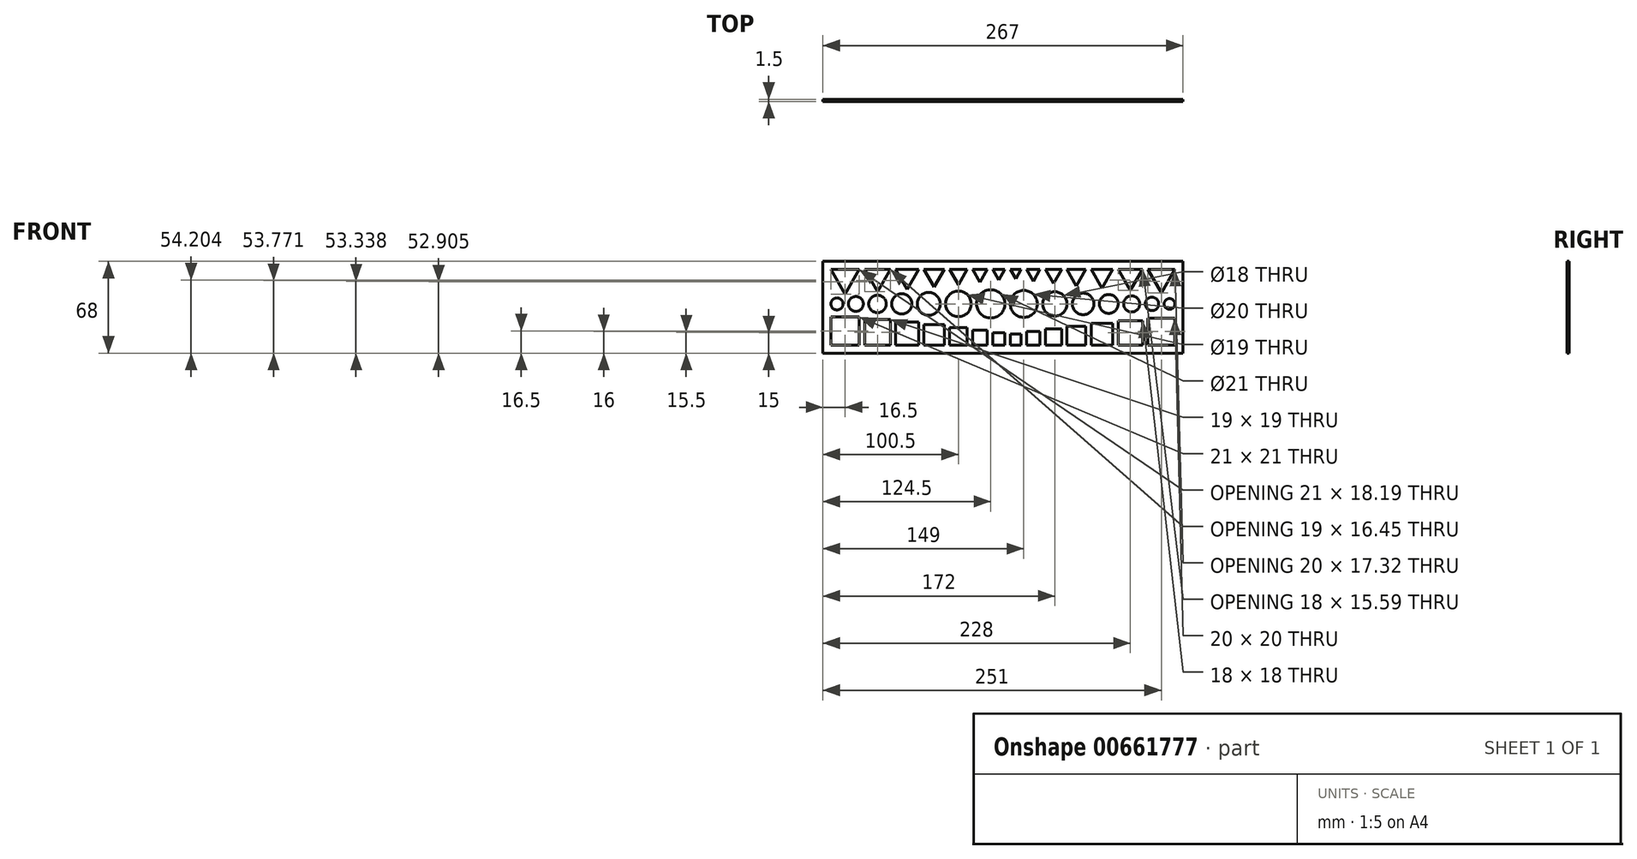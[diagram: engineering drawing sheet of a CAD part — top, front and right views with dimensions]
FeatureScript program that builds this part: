
annotation { "Feature Type Name" : "Feature", "Feature Type Description" : "" }
export const myFeature = defineFeature(function(context is Context, id is Id, definition is map)
    precondition{}
    {
        {
            var Q0;
            Q0=qCreatedBy(makeId("Front.planeOp"),FACE);
            var sketch = newSketch(context, id + "F0", { "sketchPlane" : qUnion([Q0])});
            skLineSegment(sketch, "E0.bottom", {"start": v(0, 0) * mm, "end": v(8, 0) * mm});
            skLineSegment(sketch, "E0.top", {"start": v(0, 8) * mm, "end": v(8, 8) * mm});
            skLineSegment(sketch, "E0.left", {"start": v(0, 0) * mm, "end": v(0, 8) * mm});
            skLineSegment(sketch, "E0.right", {"start": v(8, 0) * mm, "end": v(8, 8) * mm});
            skLineSegment(sketch, "E1.bottom", {"start": v(12, 0) * mm, "end": v(22, 0) * mm});
            skLineSegment(sketch, "E1.top", {"start": v(12, 10) * mm, "end": v(22, 10) * mm});
            skLineSegment(sketch, "E1.left", {"start": v(12, 0) * mm, "end": v(12, 10) * mm});
            skLineSegment(sketch, "E1.right", {"start": v(22, 0) * mm, "end": v(22, 10) * mm});
            skLineSegment(sketch, "E2.bottom", {"start": v(26, 0) * mm, "end": v(38, 0) * mm});
            skLineSegment(sketch, "E2.top", {"start": v(26, 12) * mm, "end": v(38, 12) * mm});
            skLineSegment(sketch, "E2.left", {"start": v(26, 0) * mm, "end": v(26, 12) * mm});
            skLineSegment(sketch, "E2.right", {"start": v(38, 0) * mm, "end": v(38, 12) * mm});
            skLineSegment(sketch, "E3.bottom", {"start": v(42, 0) * mm, "end": v(56, 0) * mm});
            skLineSegment(sketch, "E3.top", {"start": v(42, 14) * mm, "end": v(56, 14) * mm});
            skLineSegment(sketch, "E3.left", {"start": v(42, 0) * mm, "end": v(42, 14) * mm});
            skLineSegment(sketch, "E3.right", {"start": v(56, 0) * mm, "end": v(56, 14) * mm});
            skLineSegment(sketch, "E4.bottom", {"start": v(60, 0) * mm, "end": v(76, 0) * mm});
            skLineSegment(sketch, "E4.top", {"start": v(60, 16) * mm, "end": v(76, 16) * mm});
            skLineSegment(sketch, "E4.left", {"start": v(60, 0) * mm, "end": v(60, 16) * mm});
            skLineSegment(sketch, "E4.right", {"start": v(76, 0) * mm, "end": v(76, 16) * mm});
            skLineSegment(sketch, "E5.bottom", {"start": v(80, 0) * mm, "end": v(98, 0) * mm});
            skLineSegment(sketch, "E5.top", {"start": v(80, 18) * mm, "end": v(98, 18) * mm});
            skLineSegment(sketch, "E5.left", {"start": v(80, 0) * mm, "end": v(80, 18) * mm});
            skLineSegment(sketch, "E5.right", {"start": v(98, 0) * mm, "end": v(98, 18) * mm});
            skLineSegment(sketch, "E6.bottom", {"start": v(102, 0) * mm, "end": v(122, 0) * mm});
            skLineSegment(sketch, "E6.top", {"start": v(102, 20) * mm, "end": v(122, 20) * mm});
            skLineSegment(sketch, "E6.left", {"start": v(102, 0) * mm, "end": v(102, 20) * mm});
            skLineSegment(sketch, "E6.right", {"start": v(122, 0) * mm, "end": v(122, 20) * mm});
            skCircle(sketch, "E7", {"center": v(118, 30.5) * mm, "radius": 4 * mm});
            skCircle(sketch, "E8", {"center": v(105, 30.5) * mm, "radius": 5 * mm});
            skCircle(sketch, "E9", {"center": v(73, 30.5) * mm, "radius": 7 * mm});
            skCircle(sketch, "E10", {"center": v(90, 30.5) * mm, "radius": 6 * mm});
            skCircle(sketch, "E11", {"center": v(54, 30.5) * mm, "radius": 8 * mm});
            skCircle(sketch, "E12", {"center": v(33, 30.5) * mm, "radius": 9 * mm});
            skCircle(sketch, "E13", {"center": v(10, 30.5) * mm, "radius": 10 * mm});
            skLineSegment(sketch, "E14.bottom", {"start": v(-4, 0) * mm, "end": v(-13, 0) * mm});
            skLineSegment(sketch, "E14.top", {"start": v(-4, 9) * mm, "end": v(-13, 9) * mm});
            skLineSegment(sketch, "E14.left", {"start": v(-4, 0) * mm, "end": v(-4, 9) * mm});
            skLineSegment(sketch, "E14.right", {"start": v(-13, 0) * mm, "end": v(-13, 9) * mm});
            skLineSegment(sketch, "E15.bottom", {"start": v(-17, 0) * mm, "end": v(-28, 0) * mm});
            skLineSegment(sketch, "E15.top", {"start": v(-17, 11) * mm, "end": v(-28, 11) * mm});
            skLineSegment(sketch, "E15.left", {"start": v(-17, 0) * mm, "end": v(-17, 11) * mm});
            skLineSegment(sketch, "E15.right", {"start": v(-28, 0) * mm, "end": v(-28, 11) * mm});
            skLineSegment(sketch, "E16.bottom", {"start": v(-32, 0) * mm, "end": v(-45, 0) * mm});
            skLineSegment(sketch, "E16.top", {"start": v(-32, 13) * mm, "end": v(-45, 13) * mm});
            skLineSegment(sketch, "E16.left", {"start": v(-32, 0) * mm, "end": v(-32, 13) * mm});
            skLineSegment(sketch, "E16.right", {"start": v(-45, 0) * mm, "end": v(-45, 13) * mm});
            skLineSegment(sketch, "E17.bottom", {"start": v(-49, 0) * mm, "end": v(-64, 0) * mm});
            skLineSegment(sketch, "E17.top", {"start": v(-49, 15) * mm, "end": v(-64, 15) * mm});
            skLineSegment(sketch, "E17.left", {"start": v(-49, 0) * mm, "end": v(-49, 15) * mm});
            skLineSegment(sketch, "E17.right", {"start": v(-64, 0) * mm, "end": v(-64, 15) * mm});
            skLineSegment(sketch, "E18.bottom", {"start": v(-68, 0) * mm, "end": v(-85, 0) * mm});
            skLineSegment(sketch, "E18.top", {"start": v(-68, 17) * mm, "end": v(-85, 17) * mm});
            skLineSegment(sketch, "E18.left", {"start": v(-68, 0) * mm, "end": v(-68, 17) * mm});
            skLineSegment(sketch, "E18.right", {"start": v(-85, 0) * mm, "end": v(-85, 17) * mm});
            skLineSegment(sketch, "E19.bottom", {"start": v(-89, 0) * mm, "end": v(-108, 0) * mm});
            skLineSegment(sketch, "E19.top", {"start": v(-89, 19) * mm, "end": v(-108, 19) * mm});
            skLineSegment(sketch, "E19.left", {"start": v(-89, 0) * mm, "end": v(-89, 19) * mm});
            skLineSegment(sketch, "E19.right", {"start": v(-108, 0) * mm, "end": v(-108, 19) * mm});
            skLineSegment(sketch, "E20.bottom", {"start": v(-112, 0) * mm, "end": v(-133, 0) * mm});
            skLineSegment(sketch, "E20.top", {"start": v(-112, 21) * mm, "end": v(-133, 21) * mm});
            skLineSegment(sketch, "E20.left", {"start": v(-112, 0) * mm, "end": v(-112, 21) * mm});
            skLineSegment(sketch, "E20.right", {"start": v(-133, 0) * mm, "end": v(-133, 21) * mm});
            skCircle(sketch, "E21", {"center": v(-38.5, 30.5) * mm, "radius": 9.5 * mm});
            skCircle(sketch, "E22", {"center": v(-60.5, 30.5) * mm, "radius": 8.5 * mm});
            skCircle(sketch, "E23", {"center": v(-80.5, 30.5) * mm, "radius": 7.5 * mm});
            skCircle(sketch, "E24", {"center": v(-128.5, 30.5) * mm, "radius": 4.5 * mm});
            skCircle(sketch, "E25", {"center": v(-98.5, 30.5) * mm, "radius": 6.5 * mm});
            skCircle(sketch, "E26", {"center": v(-114.5, 30.5) * mm, "radius": 5.5 * mm});
            skCircle(sketch, "E27", {"center": v(-14.5, 30.5) * mm, "radius": 10.5 * mm});
            skCircle(sketch, "E28.cCircle", {"center": v(4, 53.69) * mm, "radius": 2.3 * mm, "construction": true});
            skLineSegment(sketch, "E28.0", {"start": v(0, 56) * mm, "end": v(8, 56) * mm});
            skLineSegment(sketch, "E28.1", {"start": v(8, 56) * mm, "end": v(4, 49.07) * mm});
            skLineSegment(sketch, "E28.2", {"start": v(4, 49.07) * mm, "end": v(0, 56) * mm});
            skPoint(sketch, "E28.0.midPoint", {"position": v(4, 56) * mm});
            skCircle(sketch, "E29.cCircle", {"center": v(17, 53.11) * mm, "radius": 2.89 * mm, "construction": true});
            skLineSegment(sketch, "E29.0", {"start": v(12, 56) * mm, "end": v(22, 56) * mm});
            skLineSegment(sketch, "E29.1", {"start": v(22, 56) * mm, "end": v(17, 47.34) * mm});
            skLineSegment(sketch, "E29.2", {"start": v(17, 47.34) * mm, "end": v(12, 56) * mm});
            skPoint(sketch, "E29.0.midPoint", {"position": v(17, 56) * mm});
            skCircle(sketch, "E30.cCircle", {"center": v(32, 52.53) * mm, "radius": 3.46 * mm, "construction": true});
            skLineSegment(sketch, "E30.0", {"start": v(26, 56) * mm, "end": v(38, 56) * mm});
            skLineSegment(sketch, "E30.1", {"start": v(38, 56) * mm, "end": v(32, 45.6) * mm});
            skLineSegment(sketch, "E30.2", {"start": v(32, 45.6) * mm, "end": v(26, 56) * mm});
            skPoint(sketch, "E30.0.midPoint", {"position": v(32, 56) * mm});
            skCircle(sketch, "E31.cCircle", {"center": v(49, 51.96) * mm, "radius": 4.04 * mm, "construction": true});
            skLineSegment(sketch, "E31.0", {"start": v(42, 56) * mm, "end": v(56, 56) * mm});
            skLineSegment(sketch, "E31.1", {"start": v(56, 56) * mm, "end": v(49, 43.87) * mm});
            skLineSegment(sketch, "E31.2", {"start": v(49, 43.87) * mm, "end": v(42, 56) * mm});
            skPoint(sketch, "E31.0.midPoint", {"position": v(49, 56) * mm});
            skCircle(sketch, "E32.cCircle", {"center": v(68, 51.38) * mm, "radius": 4.62 * mm, "construction": true});
            skLineSegment(sketch, "E32.0", {"start": v(60, 56) * mm, "end": v(76, 56) * mm});
            skLineSegment(sketch, "E32.1", {"start": v(76, 56) * mm, "end": v(68, 42.14) * mm});
            skLineSegment(sketch, "E32.2", {"start": v(68, 42.14) * mm, "end": v(60, 56) * mm});
            skPoint(sketch, "E32.0.midPoint", {"position": v(68, 56) * mm});
            skCircle(sketch, "E33.cCircle", {"center": v(89, 50.8) * mm, "radius": 5.2 * mm, "construction": true});
            skLineSegment(sketch, "E33.0", {"start": v(80, 56) * mm, "end": v(98, 56) * mm});
            skLineSegment(sketch, "E33.1", {"start": v(98, 56) * mm, "end": v(89, 40.4) * mm});
            skLineSegment(sketch, "E33.2", {"start": v(89, 40.4) * mm, "end": v(80, 56) * mm});
            skPoint(sketch, "E33.0.midPoint", {"position": v(89, 56) * mm});
            skCircle(sketch, "E34.cCircle", {"center": v(112, 50.22) * mm, "radius": 5.77 * mm, "construction": true});
            skLineSegment(sketch, "E34.0", {"start": v(102, 56) * mm, "end": v(122, 56) * mm});
            skLineSegment(sketch, "E34.1", {"start": v(122, 56) * mm, "end": v(112, 38.68) * mm});
            skLineSegment(sketch, "E34.2", {"start": v(112, 38.68) * mm, "end": v(102, 56) * mm});
            skPoint(sketch, "E34.0.midPoint", {"position": v(112, 56) * mm});
            skCircle(sketch, "E35.cCircle", {"center": v(-8.5, 53.4) * mm, "radius": 2.6 * mm, "construction": true});
            skLineSegment(sketch, "E35.0", {"start": v(-13, 56) * mm, "end": v(-4, 56) * mm});
            skLineSegment(sketch, "E35.1", {"start": v(-4, 56) * mm, "end": v(-8.5, 48.2) * mm});
            skLineSegment(sketch, "E35.2", {"start": v(-8.5, 48.2) * mm, "end": v(-13, 56) * mm});
            skPoint(sketch, "E35.0.midPoint", {"position": v(-8.5, 56) * mm});
            skCircle(sketch, "E36.cCircle", {"center": v(-22.5, 52.82) * mm, "radius": 3.18 * mm, "construction": true});
            skLineSegment(sketch, "E36.0", {"start": v(-28, 56) * mm, "end": v(-17, 56) * mm});
            skLineSegment(sketch, "E36.1", {"start": v(-17, 56) * mm, "end": v(-22.5, 46.47) * mm});
            skLineSegment(sketch, "E36.2", {"start": v(-22.5, 46.47) * mm, "end": v(-28, 56) * mm});
            skPoint(sketch, "E36.0.midPoint", {"position": v(-22.5, 56) * mm});
            skCircle(sketch, "E37.cCircle", {"center": v(-38.5, 52.25) * mm, "radius": 3.75 * mm, "construction": true});
            skLineSegment(sketch, "E37.0", {"start": v(-45, 56) * mm, "end": v(-32, 56) * mm});
            skLineSegment(sketch, "E37.1", {"start": v(-32, 56) * mm, "end": v(-38.5, 44.74) * mm});
            skLineSegment(sketch, "E37.2", {"start": v(-38.5, 44.74) * mm, "end": v(-45, 56) * mm});
            skPoint(sketch, "E37.0.midPoint", {"position": v(-38.5, 56) * mm});
            skCircle(sketch, "E38.cCircle", {"center": v(-56.5, 51.67) * mm, "radius": 4.33 * mm, "construction": true});
            skLineSegment(sketch, "E38.0", {"start": v(-64, 56) * mm, "end": v(-49, 56) * mm});
            skLineSegment(sketch, "E38.1", {"start": v(-49, 56) * mm, "end": v(-56.5, 43) * mm});
            skLineSegment(sketch, "E38.2", {"start": v(-56.5, 43) * mm, "end": v(-64, 56) * mm});
            skPoint(sketch, "E38.0.midPoint", {"position": v(-56.5, 56) * mm});
            skCircle(sketch, "E39.cCircle", {"center": v(-76.5, 51.1) * mm, "radius": 4.9 * mm, "construction": true});
            skLineSegment(sketch, "E39.0", {"start": v(-85, 56) * mm, "end": v(-68, 56) * mm});
            skLineSegment(sketch, "E39.1", {"start": v(-68, 56) * mm, "end": v(-76.5, 41.28) * mm});
            skLineSegment(sketch, "E39.2", {"start": v(-76.5, 41.28) * mm, "end": v(-85, 56) * mm});
            skPoint(sketch, "E39.0.midPoint", {"position": v(-76.5, 56) * mm});
            skCircle(sketch, "E40.cCircle", {"center": v(-98.5, 50.51) * mm, "radius": 5.48 * mm, "construction": true});
            skLineSegment(sketch, "E40.0", {"start": v(-108, 56) * mm, "end": v(-89, 56) * mm});
            skLineSegment(sketch, "E40.1", {"start": v(-89, 56) * mm, "end": v(-98.5, 39.54) * mm});
            skLineSegment(sketch, "E40.2", {"start": v(-98.5, 39.54) * mm, "end": v(-108, 56) * mm});
            skPoint(sketch, "E40.0.midPoint", {"position": v(-98.5, 56) * mm});
            skCircle(sketch, "E41.cCircle", {"center": v(-122.5, 49.94) * mm, "radius": 6.06 * mm, "construction": true});
            skLineSegment(sketch, "E41.0", {"start": v(-133, 56) * mm, "end": v(-112, 56) * mm});
            skLineSegment(sketch, "E41.1", {"start": v(-112, 56) * mm, "end": v(-122.5, 37.81) * mm});
            skLineSegment(sketch, "E41.2", {"start": v(-122.5, 37.81) * mm, "end": v(-133, 56) * mm});
            skPoint(sketch, "E41.0.midPoint", {"position": v(-122.5, 56) * mm});
            skLineSegment(sketch, "E42.bottom", {"start": v(-139, 62) * mm, "end": v(128, 62) * mm});
            skLineSegment(sketch, "E42.top", {"start": v(-139, -6) * mm, "end": v(128, -6) * mm});
            skLineSegment(sketch, "E42.left", {"start": v(-139, 62) * mm, "end": v(-139, -6) * mm});
            skLineSegment(sketch, "E42.right", {"start": v(128, 62) * mm, "end": v(128, -6) * mm});
            skSolve(sketch);
        }
        {
            var Q0;
            Q0 = qSketchRegion(id + "F0", true);
            extrude(context, id + "F1", {"entities" : qUnion([Q0]), "depth" : 1.5 * mm, "offsetDistance" : 25 * mm});
        }
    });
